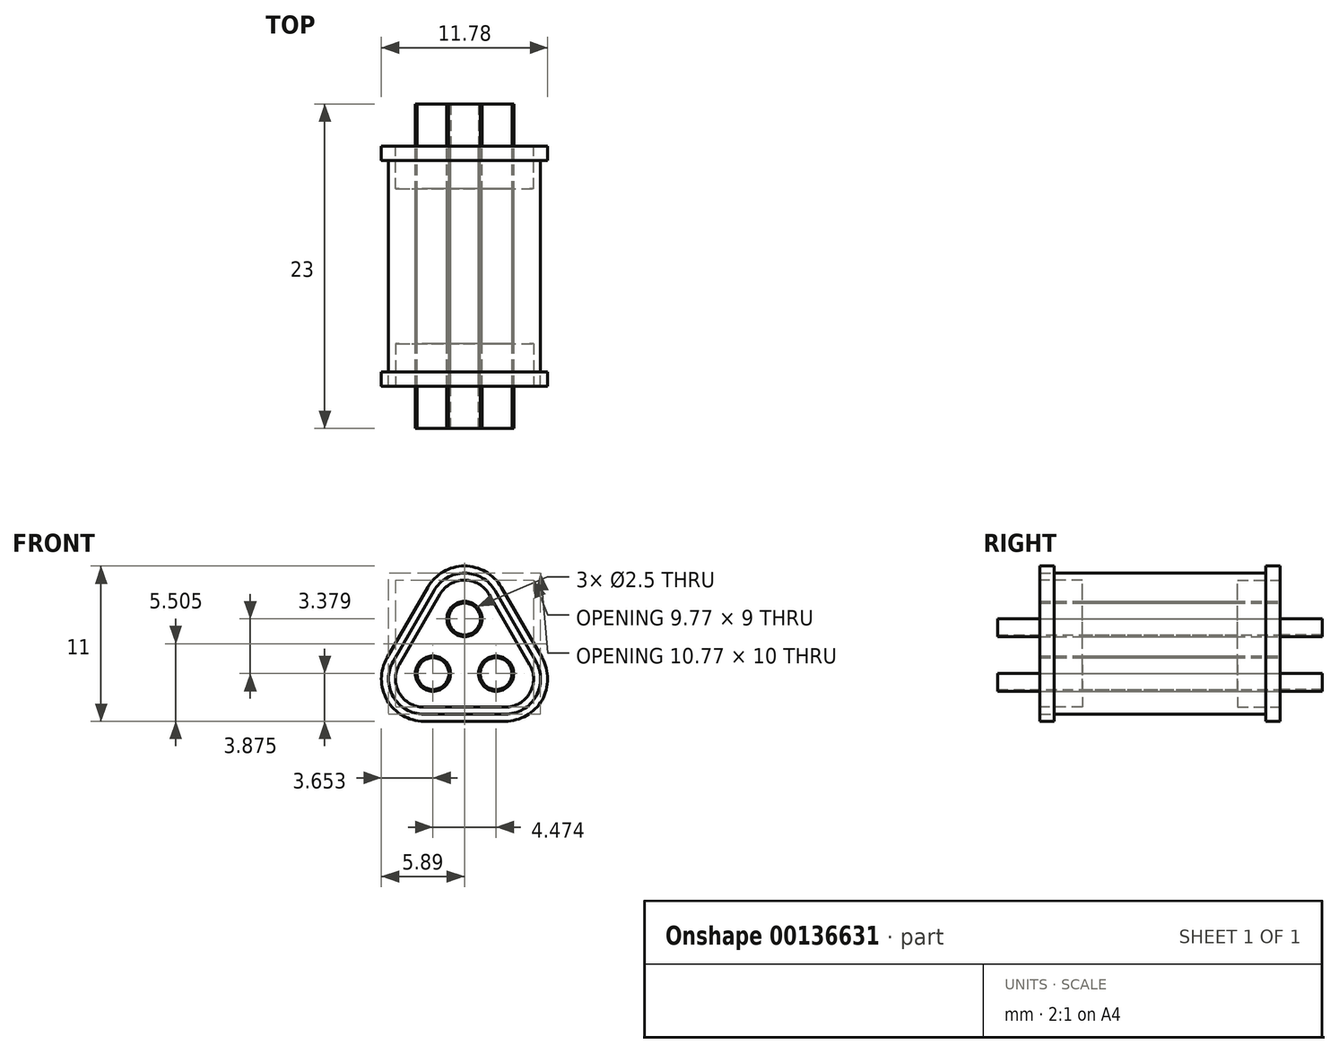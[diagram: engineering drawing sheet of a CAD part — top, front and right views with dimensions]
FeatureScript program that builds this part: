
annotation { "Feature Type Name" : "Feature", "Feature Type Description" : "" }
export const myFeature = defineFeature(function(context is Context, id is Id, definition is map)
    precondition{}
    {
        {
            var Q0;
            Q0=qCreatedBy(makeId("Front.planeOp"),FACE);
            var sketch = newSketch(context, id + "F0", { "sketchPlane" : qUnion([Q0])});
            skLineSegment(sketch, "E0", {"start": v(-5.05, -1.5) * mm, "end": v(-2.17, 3.5) * mm});
            skLineSegment(sketch, "E1", {"start": v(2.17, 3.5) * mm, "end": v(5.05, -1.5) * mm});
            skLineSegment(sketch, "E2", {"start": v(2.89, -5.26) * mm, "end": v(-2.89, -5.26) * mm});
            skPoint(sketch, "E3.visualSharp", {"position": v(-7.22, -5.26) * mm});
            skArc(sketch, "E3.filletArc", {"start": v(-5.05, -1.5) * mm, "mid": v(-5.05, -4) * mm, "end": v(-2.89, -5.26) * mm});
            skPoint(sketch, "E4.visualSharp", {"position": v(7.22, -5.26) * mm});
            skArc(sketch, "E4.filletArc", {"start": v(2.89, -5.26) * mm, "mid": v(5.05, -4) * mm, "end": v(5.05, -1.5) * mm});
            skPoint(sketch, "E5.visualSharp", {"position": v(0, 7.24) * mm});
            skArc(sketch, "E5.filletArc", {"start": v(2.17, 3.5) * mm, "mid": v(0, 4.74) * mm, "end": v(-2.17, 3.5) * mm});
            skArc(sketch, "E6.0", {"start": v(-5.48, -1.26) * mm, "mid": v(-5.48, -4.26) * mm, "end": v(-2.89, -5.76) * mm});
            skArc(sketch, "E6.1", {"start": v(2.6, 3.74) * mm, "mid": v(0, 5.24) * mm, "end": v(-2.6, 3.74) * mm});
            skLineSegment(sketch, "E6.2", {"start": v(2.6, 3.74) * mm, "end": v(5.48, -1.26) * mm});
            skLineSegment(sketch, "E6.3", {"start": v(-5.48, -1.26) * mm, "end": v(-2.6, 3.74) * mm});
            skArc(sketch, "E6.4", {"start": v(2.89, -5.76) * mm, "mid": v(5.48, -4.26) * mm, "end": v(5.48, -1.26) * mm});
            skLineSegment(sketch, "E6.5", {"start": v(2.89, -5.76) * mm, "end": v(-2.89, -5.76) * mm});
            skArc(sketch, "E7.0", {"start": v(-4.62, -1.76) * mm, "mid": v(-4.62, -3.76) * mm, "end": v(-2.89, -4.76) * mm});
            skArc(sketch, "E7.1", {"start": v(1.73, 3.24) * mm, "mid": v(0, 4.24) * mm, "end": v(-1.73, 3.24) * mm});
            skLineSegment(sketch, "E7.2", {"start": v(1.73, 3.24) * mm, "end": v(4.62, -1.76) * mm});
            skLineSegment(sketch, "E7.3", {"start": v(-4.62, -1.76) * mm, "end": v(-1.73, 3.24) * mm});
            skArc(sketch, "E7.4", {"start": v(2.89, -4.76) * mm, "mid": v(4.62, -3.76) * mm, "end": v(4.62, -1.76) * mm});
            skLineSegment(sketch, "E7.5", {"start": v(2.89, -4.76) * mm, "end": v(-2.89, -4.76) * mm});
            skLineSegment(sketch, "E8", {"start": v(0, 2.24) * mm, "end": v(0, -3.86) * mm, "construction": true});
            skCircle(sketch, "E9", {"center": v(2.24, -2.38) * mm, "radius": 1.25 * mm});
            skCircle(sketch, "E10", {"center": v(0, 1.5) * mm, "radius": 1.25 * mm});
            skCircle(sketch, "E11", {"center": v(-2.24, -2.38) * mm, "radius": 1.25 * mm});
            skCircle(sketch, "E12.0", {"center": v(2.24, -2.38) * mm, "radius": 1.12 * mm});
            skCircle(sketch, "E13.0", {"center": v(0, 1.5) * mm, "radius": 1.13 * mm});
            skCircle(sketch, "E14.0", {"center": v(-2.24, -2.38) * mm, "radius": 1.13 * mm});
            skLineSegment(sketch, "E15", {"start": v(1.13, 1.5) * mm, "end": v(1.25, 1.5) * mm});
            skLineSegment(sketch, "E16", {"start": v(-1.12, 1.5) * mm, "end": v(-1.25, 1.5) * mm});
            skLineSegment(sketch, "E17", {"start": v(-1.11, -2.38) * mm, "end": v(-0.99, -2.38) * mm});
            skLineSegment(sketch, "E18", {"start": v(-3.36, -2.38) * mm, "end": v(-3.49, -2.38) * mm});
            skLineSegment(sketch, "E19", {"start": v(3.36, -2.38) * mm, "end": v(3.49, -2.38) * mm});
            skLineSegment(sketch, "E20", {"start": v(1.11, -2.38) * mm, "end": v(0.99, -2.38) * mm});
            skSolve(sketch);
        }
        {
            var Q0;
            Q0=makeQuery(id+"F0.imprint","IMPRINT",FACE,{"disambiguationData":[TD([[makeQuery(id+"F0.imprint","IMPRINT",EDGE,{"derivedFrom":sQuery(id+"F0.wireOp",EDGE,"E0")}),-1.0]])]});
            var Q1;
            Q1=makeQuery(id+"F0.imprint","IMPRINT",FACE,{"disambiguationData":[TD([[makeQuery(id+"F0.imprint","IMPRINT",EDGE,{"derivedFrom":sQuery(id+"F0.wireOp",EDGE,"E7.0")}),1.0]])]});
            extrude(context, id + "F1", {"entities" : qUnion([Q0, Q1]), "depth" : 17 * mm});
        }
        {
            var Q0;
            Q0=makeQuery(id+"F0.imprint","IMPRINT",FACE,{"disambiguationData":[TD([[makeQuery(id+"F0.imprint","IMPRINT",EDGE,{"derivedFrom":sQuery(id+"F0.wireOp",EDGE,"E0")}),1.0]])]});
            var Q1;
            Q1=makeQuery(id+"F1.opExtrude","CAP_FACE",FACE,{"disambiguationData":[OSD([sQuery(id+"F0.wireOp",EDGE,"E0"),sQuery(id+"F0.wireOp",EDGE,"E1"),sQuery(id+"F0.wireOp",EDGE,"E2"),sQuery(id+"F0.wireOp",EDGE,"E3.filletArc"),sQuery(id+"F0.wireOp",EDGE,"E4.filletArc"),sQuery(id+"F0.wireOp",EDGE,"E5.filletArc")])],"isStart":false});
            extrude(context, id + "F2", {"entities" : qUnion([Q0]), "operationType" : NewBodyOperationType.ADD, "depth" : 1 * mm});
        }
        {
            var Q0;
            Q0=makeQuery(id+"F0.imprint","IMPRINT",FACE,{"disambiguationData":[TD([[makeQuery(id+"F0.imprint","IMPRINT",EDGE,{"derivedFrom":sQuery(id+"F0.wireOp",EDGE,"E7.0")}),1.0]])]});
            extrude(context, id + "F3", {"entities" : qUnion([Q0]), "operationType" : NewBodyOperationType.REMOVE, "depth" : 3 * mm});
        }
        {
            var Q0;
            {var subQ0=sQuery(id+"F0.wireOp",EDGE,"E19");Q0=makeQuery(id+"F0.imprint","IMPRINT",FACE,{"disambiguationData":[TD([[makeQuery(id+"F0.imprint","IMPRINT",EDGE,{"derivedFrom":subQ0}),1.0]])]});}
            var Q1;
            {var subQ0=sQuery(id+"F0.wireOp",EDGE,"E15");Q1=makeQuery(id+"F0.imprint","IMPRINT",FACE,{"disambiguationData":[TD([[makeQuery(id+"F0.imprint","IMPRINT",EDGE,{"derivedFrom":subQ0}),1.0]])]});}
            var Q2;
            {var subQ0=sQuery(id+"F0.wireOp",EDGE,"E17");Q2=makeQuery(id+"F0.imprint","IMPRINT",FACE,{"disambiguationData":[TD([[makeQuery(id+"F0.imprint","IMPRINT",EDGE,{"derivedFrom":subQ0}),1.0]])]});}
            var Q3;
            Q3=makeQuery(id+"F3.boolean.opBoolean","COPY",FACE,{"derivedFrom":makeQuery(id+"F3.opExtrude","CAP_FACE",FACE,{"disambiguationData":[OSD([sQuery(id+"F0.wireOp",EDGE,"E7.0"),sQuery(id+"F0.wireOp",EDGE,"E7.1"),sQuery(id+"F0.wireOp",EDGE,"E7.2"),sQuery(id+"F0.wireOp",EDGE,"E7.3"),sQuery(id+"F0.wireOp",EDGE,"E7.4"),sQuery(id+"F0.wireOp",EDGE,"E7.5"),sQuery(id+"F0.wireOp",EDGE,"E9"),sQuery(id+"F0.wireOp",EDGE,"E10"),sQuery(id+"F0.wireOp",EDGE,"E11")])],"isStart":false})});
            extrude(context, id + "F4", {"entities" : qUnion([Q0, Q1, Q2]), "endBoundEntityFace" : qUnion([Q3]), "depth" : 17 * mm});
        }
        {
            var Q0;
            {var subQ0=sQuery(id+"F0.wireOp",EDGE,"E19");Q0=makeQuery(id+"F0.imprint","IMPRINT",FACE,{"disambiguationData":[TD([[makeQuery(id+"F0.imprint","IMPRINT",EDGE,{"derivedFrom":subQ0}),-1.0]])]});}
            var Q1;
            {var subQ0=sQuery(id+"F0.wireOp",EDGE,"E17");Q1=makeQuery(id+"F0.imprint","IMPRINT",FACE,{"disambiguationData":[TD([[makeQuery(id+"F0.imprint","IMPRINT",EDGE,{"derivedFrom":subQ0}),-1.0]])]});}
            var Q2;
            {var subQ0=sQuery(id+"F0.wireOp",EDGE,"E15");Q2=makeQuery(id+"F0.imprint","IMPRINT",FACE,{"disambiguationData":[TD([[makeQuery(id+"F0.imprint","IMPRINT",EDGE,{"derivedFrom":subQ0}),-1.0]])]});}
            extrude(context, id + "F5", {"entities" : qUnion([Q0, Q1, Q2]), "depth" : 20 * mm});
        }
        {
            var Q0;
            {var subQ0=sQuery(id+"F0.wireOp",EDGE,"E13.0");var subQ1=makeQuery(id+"F0.imprint","INTERSECT",VERTEX,{"derivedFrom":[subQ0,sQuery(id+"F0.wireOp",EDGE,"E15")]});Q0=makeQuery(id+"F0.imprint","IMPRINT",FACE,{"disambiguationData":[TD([[makeQuery(id+"F0.imprint","IMPRINT",EDGE,{"disambiguationData":[TD([[subQ1,-1.0]])],"derivedFrom":subQ0}),1.0]])]});}
            var Q1;
            {var subQ0=sQuery(id+"F0.wireOp",EDGE,"E12.0");var subQ1=makeQuery(id+"F0.imprint","INTERSECT",VERTEX,{"derivedFrom":[subQ0,sQuery(id+"F0.wireOp",EDGE,"E19")]});Q1=makeQuery(id+"F0.imprint","IMPRINT",FACE,{"disambiguationData":[TD([[makeQuery(id+"F0.imprint","IMPRINT",EDGE,{"disambiguationData":[TD([[subQ1,-1.0]])],"derivedFrom":subQ0}),1.0]])]});}
            var Q2;
            {var subQ0=sQuery(id+"F0.wireOp",EDGE,"E14.0");var subQ1=makeQuery(id+"F0.imprint","INTERSECT",VERTEX,{"derivedFrom":[subQ0,sQuery(id+"F0.wireOp",EDGE,"E17")]});Q2=makeQuery(id+"F0.imprint","IMPRINT",FACE,{"disambiguationData":[TD([[makeQuery(id+"F0.imprint","IMPRINT",EDGE,{"disambiguationData":[TD([[subQ1,-1.0]])],"derivedFrom":subQ0}),1.0]])]});}
            extrude(context, id + "F6", {"entities" : qUnion([Q0, Q1, Q2]), "depth" : 14 * mm});
        }
        {
            var Q0;
            {var subQ0=sQuery(id+"F0.wireOp",EDGE,"E13.0");var subQ1=makeQuery(id+"F0.imprint","INTERSECT",VERTEX,{"derivedFrom":[subQ0,sQuery(id+"F0.wireOp",EDGE,"E15")]});Q0=makeQuery(id+"F0.imprint","IMPRINT",FACE,{"disambiguationData":[TD([[makeQuery(id+"F0.imprint","IMPRINT",EDGE,{"disambiguationData":[TD([[subQ1,-1.0]])],"derivedFrom":subQ0}),1.0]])]});}
            var Q1;
            {var subQ0=sQuery(id+"F0.wireOp",EDGE,"E14.0");var subQ1=makeQuery(id+"F0.imprint","INTERSECT",VERTEX,{"derivedFrom":[subQ0,sQuery(id+"F0.wireOp",EDGE,"E17")]});Q1=makeQuery(id+"F0.imprint","IMPRINT",FACE,{"disambiguationData":[TD([[makeQuery(id+"F0.imprint","IMPRINT",EDGE,{"disambiguationData":[TD([[subQ1,-1.0]])],"derivedFrom":subQ0}),1.0]])]});}
            var Q2;
            {var subQ0=sQuery(id+"F0.wireOp",EDGE,"E12.0");var subQ1=makeQuery(id+"F0.imprint","INTERSECT",VERTEX,{"derivedFrom":[subQ0,sQuery(id+"F0.wireOp",EDGE,"E19")]});Q2=makeQuery(id+"F0.imprint","IMPRINT",FACE,{"disambiguationData":[TD([[makeQuery(id+"F0.imprint","IMPRINT",EDGE,{"disambiguationData":[TD([[subQ1,-1.0]])],"derivedFrom":subQ0}),1.0]])]});}
            var Q3;
            Q3=makeQuery(id+"F3.boolean.opBoolean","COPY",FACE,{"derivedFrom":makeQuery(id+"F3.opExtrude","CAP_FACE",FACE,{"disambiguationData":[OSD([sQuery(id+"F0.wireOp",EDGE,"E7.0"),sQuery(id+"F0.wireOp",EDGE,"E7.1"),sQuery(id+"F0.wireOp",EDGE,"E7.2"),sQuery(id+"F0.wireOp",EDGE,"E7.3"),sQuery(id+"F0.wireOp",EDGE,"E7.4"),sQuery(id+"F0.wireOp",EDGE,"E7.5"),sQuery(id+"F0.wireOp",EDGE,"E9"),sQuery(id+"F0.wireOp",EDGE,"E10"),sQuery(id+"F0.wireOp",EDGE,"E11")])],"isStart":false})});
            extrude(context, id + "F7", {"entities" : qUnion([Q0, Q1, Q2]), "operationType" : NewBodyOperationType.REMOVE, "endBound" : BoundingType.UP_TO_SURFACE, "endBoundEntityFace" : qUnion([Q3]), "depth" : 25 * mm});
        }
        {
            var Q0;
            {var subQ0=sQuery(id+"F0.wireOp",EDGE,"E19");Q0=makeQuery(id+"F0.imprint","IMPRINT",FACE,{"disambiguationData":[TD([[makeQuery(id+"F0.imprint","IMPRINT",EDGE,{"derivedFrom":subQ0}),-1.0]])]});}
            var Q1;
            {var subQ0=sQuery(id+"F0.wireOp",EDGE,"E17");Q1=makeQuery(id+"F0.imprint","IMPRINT",FACE,{"disambiguationData":[TD([[makeQuery(id+"F0.imprint","IMPRINT",EDGE,{"derivedFrom":subQ0}),-1.0]])]});}
            var Q2;
            {var subQ0=sQuery(id+"F0.wireOp",EDGE,"E15");Q2=makeQuery(id+"F0.imprint","IMPRINT",FACE,{"disambiguationData":[TD([[makeQuery(id+"F0.imprint","IMPRINT",EDGE,{"derivedFrom":subQ0}),-1.0]])]});}
            extrude(context, id + "F8", {"entities" : qUnion([Q0, Q1, Q2]), "oppositeDirection" : true, "depth" : 3 * mm});
        }
        {
            var Q0;
            Q0=makeQuery(id+"F1.opExtrude","CAP_FACE",FACE,{"disambiguationData":[OSD([sQuery(id+"F0.wireOp",EDGE,"E0"),sQuery(id+"F0.wireOp",EDGE,"E1"),sQuery(id+"F0.wireOp",EDGE,"E2"),sQuery(id+"F0.wireOp",EDGE,"E3.filletArc"),sQuery(id+"F0.wireOp",EDGE,"E4.filletArc"),sQuery(id+"F0.wireOp",EDGE,"E5.filletArc"),sQuery(id+"F0.wireOp",EDGE,"E9"),sQuery(id+"F0.wireOp",EDGE,"E10"),sQuery(id+"F0.wireOp",EDGE,"E11")])],"isStart":false});
            var sketch = newSketch(context, id + "F9", { "sketchPlane" : qUnion([Q0])});
            skArc(sketch, "E21.0", {"start": v(-5.48, -1.26) * mm, "mid": v(-5.48, -4.26) * mm, "end": v(-2.89, -5.76) * mm});
            skArc(sketch, "E21.1", {"start": v(2.6, 3.74) * mm, "mid": v(0, 5.24) * mm, "end": v(-2.6, 3.74) * mm});
            skLineSegment(sketch, "E21.2", {"start": v(2.6, 3.74) * mm, "end": v(5.48, -1.26) * mm});
            skLineSegment(sketch, "E21.3", {"start": v(-5.48, -1.26) * mm, "end": v(-2.6, 3.74) * mm});
            skArc(sketch, "E21.4", {"start": v(2.89, -5.76) * mm, "mid": v(5.48, -4.26) * mm, "end": v(5.48, -1.26) * mm});
            skLineSegment(sketch, "E21.5", {"start": v(2.89, -5.76) * mm, "end": v(-2.89, -5.76) * mm});
            skArc(sketch, "E22.0", {"start": v(-4.62, -1.76) * mm, "mid": v(-4.62, -3.76) * mm, "end": v(-2.89, -4.76) * mm});
            skArc(sketch, "E22.1", {"start": v(1.73, 3.24) * mm, "mid": v(0, 4.24) * mm, "end": v(-1.73, 3.24) * mm});
            skLineSegment(sketch, "E22.2", {"start": v(1.73, 3.24) * mm, "end": v(4.62, -1.76) * mm});
            skLineSegment(sketch, "E22.3", {"start": v(-4.62, -1.76) * mm, "end": v(-1.73, 3.24) * mm});
            skArc(sketch, "E22.4", {"start": v(2.89, -4.76) * mm, "mid": v(4.62, -3.76) * mm, "end": v(4.62, -1.76) * mm});
            skLineSegment(sketch, "E22.5", {"start": v(2.89, -4.76) * mm, "end": v(-2.89, -4.76) * mm});
            skSolve(sketch);
        }
        {
            var Q0;
            Q0=makeQuery(id+"F9.imprint","IMPRINT",FACE,{"disambiguationData":[TD([[makeQuery(id+"F9.imprint","IMPRINT",EDGE,{"derivedFrom":sQuery(id+"F9.wireOp",EDGE,"E21.0")}),1.0]])]});
            extrude(context, id + "F10", {"entities" : qUnion([Q0]), "oppositeDirection" : true, "depth" : 1 * mm});
        }
        {
            var Q0;
            Q0=makeQuery(id+"F9.imprint","IMPRINT",FACE,{"disambiguationData":[TD([[makeQuery(id+"F9.imprint","IMPRINT",EDGE,{"derivedFrom":sQuery(id+"F9.wireOp",EDGE,"E22.0")}),1.0]])]});
            extrude(context, id + "F11", {"entities" : qUnion([Q0]), "operationType" : NewBodyOperationType.REMOVE, "oppositeDirection" : true, "depth" : 3 * mm});
        }
    });
